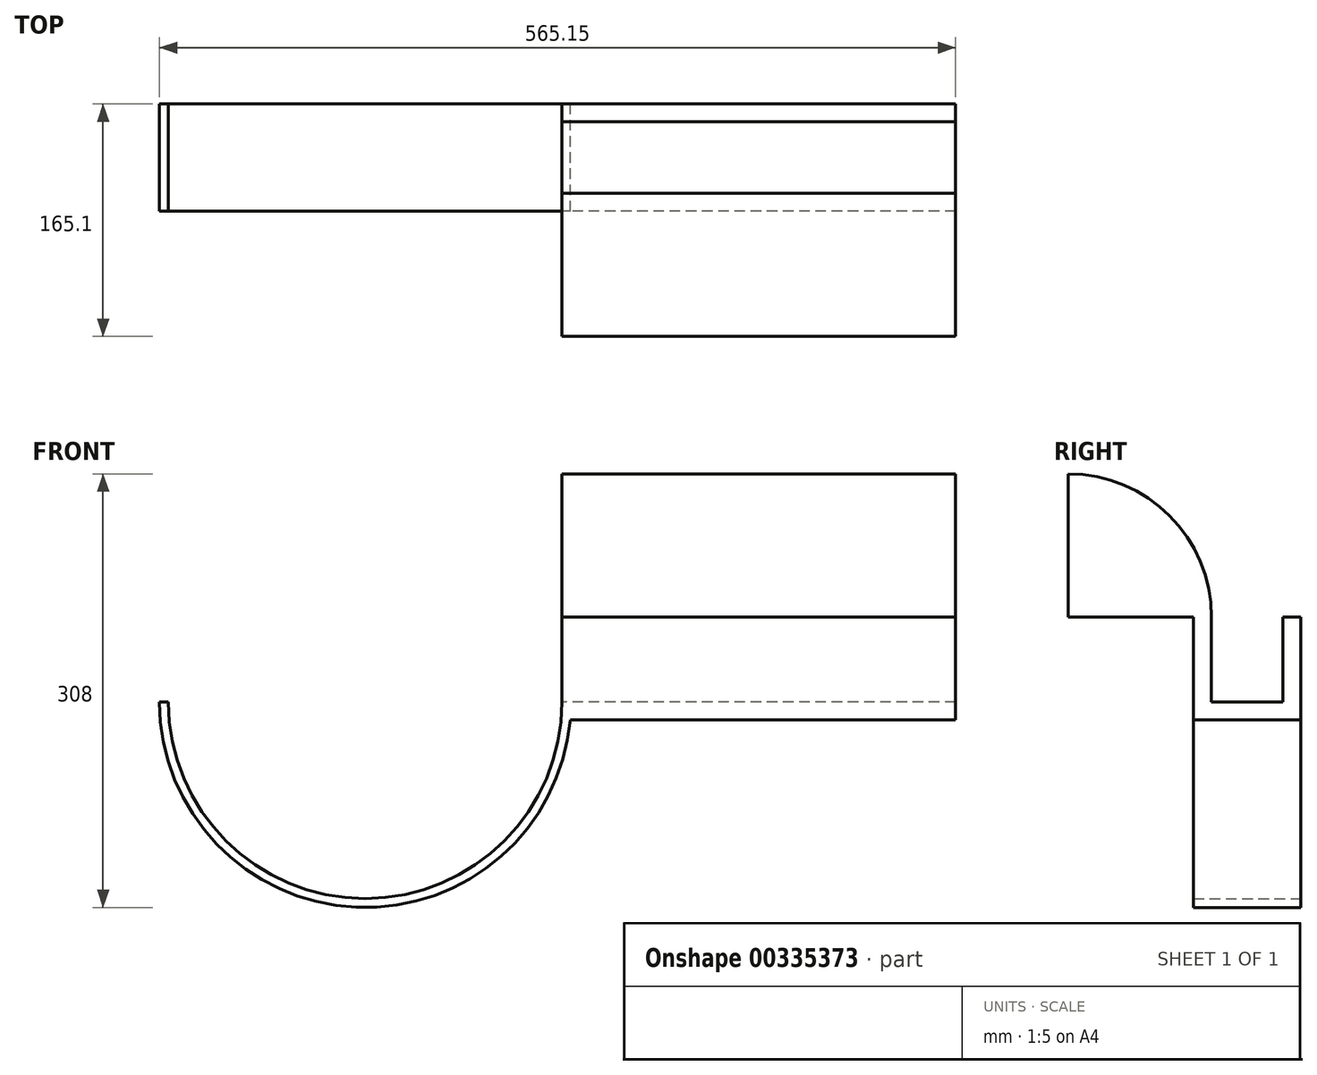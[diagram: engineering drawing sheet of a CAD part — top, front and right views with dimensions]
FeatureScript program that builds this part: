
annotation { "Feature Type Name" : "Feature", "Feature Type Description" : "" }
export const myFeature = defineFeature(function(context is Context, id is Id, definition is map)
    precondition{}
    {
        {
            var Q0;
            Q0=qCreatedBy(makeId("Right.planeOp"),FACE);
            var sketch = newSketch(context, id + "F0", { "sketchPlane" : qUnion([Q0])});
            skLineSegment(sketch, "E0", {"start": v(-101.6, -215.67) * mm, "end": v(-12.7, -215.67) * mm});
            skLineSegment(sketch, "E1", {"start": v(0, -276.02) * mm, "end": v(50.8, -276.02) * mm});
            skLineSegment(sketch, "E2", {"start": v(50.8, -215.67) * mm, "end": v(50.8, -276.02) * mm});
            skLineSegment(sketch, "E3", {"start": v(0, -276.02) * mm, "end": v(0, -215.67) * mm});
            skPoint(sketch, "E4.visualSharp", {"position": v(0, -114.07) * mm});
            skArc(sketch, "E4.filletArc", {"start": v(0, -215.67) * mm, "mid": v(-29.76, -143.83) * mm, "end": v(-101.6, -114.07) * mm});
            skLineSegment(sketch, "E5", {"start": v(50.8, -215.67) * mm, "end": v(63.5, -215.67) * mm});
            skLineSegment(sketch, "E6", {"start": v(63.5, -215.67) * mm, "end": v(63.5, -288.72) * mm});
            skLineSegment(sketch, "E7", {"start": v(63.5, -288.72) * mm, "end": v(-12.7, -288.72) * mm});
            skLineSegment(sketch, "E8", {"start": v(-12.7, -288.72) * mm, "end": v(-12.7, -215.67) * mm});
            skLineSegment(sketch, "E9", {"start": v(-101.6, -114.07) * mm, "end": v(-101.6, -215.67) * mm});
            skSolve(sketch);
        }
        {
            var Q0;
            Q0=makeQuery(id+"F0.imprint","IMPRINT",FACE,{"disambiguationData":[TD([[makeQuery(id+"F0.imprint","IMPRINT",EDGE,{"derivedFrom":sQuery(id+"F0.wireOp",EDGE,"E0")}),1.0]])]});
            extrude(context, id + "F1", {"entities" : qUnion([Q0]), "depth" : 279.4 * mm});
        }
        {
            var Q0;
            Q0=makeQuery(id+"F1.opExtrude","SWEPT_FACE",FACE,{"disambiguationData":[OSD([sQuery(id+"F0.wireOp",EDGE,"E6")])]});
            var sketch = newSketch(context, id + "F2", { "sketchPlane" : qUnion([Q0])});
            skPoint(sketch, "E10", {"position": v(9.84, -275.62) * mm});
            skArc(sketch, "E11", {"start": v(0, -276.02) * mm, "mid": v(139.7, -415.72) * mm, "end": v(279.4, -276.02) * mm});
            skArc(sketch, "E12", {"start": v(-6.35, -276.02) * mm, "mid": v(139.7, -422.07) * mm, "end": v(285.75, -276.02) * mm});
            skLineSegment(sketch, "E13", {"start": v(0, -276.02) * mm, "end": v(-6.35, -276.02) * mm});
            skLineSegment(sketch, "E14", {"start": v(279.4, -276.02) * mm, "end": v(285.75, -276.02) * mm});
            skSolve(sketch);
        }
        {
            var Q0;
            Q0 = qSketchRegion(id + "F2", true);
            extrude(context, id + "F3", {"entities" : qUnion([Q0]), "operationType" : NewBodyOperationType.ADD, "oppositeDirection" : true, "depth" : 76.2 * mm});
        }
    });
